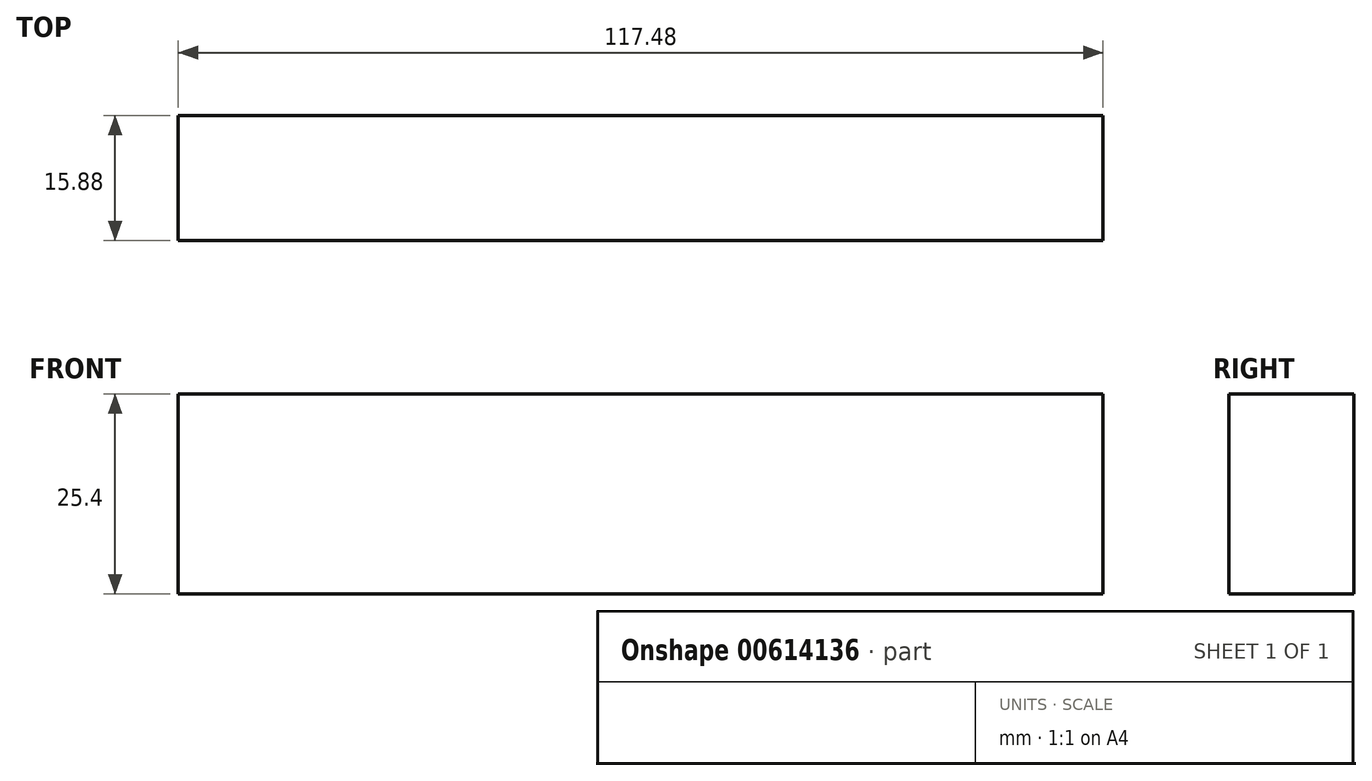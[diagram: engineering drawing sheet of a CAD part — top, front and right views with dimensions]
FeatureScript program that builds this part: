
annotation { "Feature Type Name" : "Feature", "Feature Type Description" : "" }
export const myFeature = defineFeature(function(context is Context, id is Id, definition is map)
    precondition{}
    {
        {
            var Q0;
            Q0=qCreatedBy(makeId("Top.planeOp"),FACE);
            var sketch = newSketch(context, id + "F0", { "sketchPlane" : qUnion([Q0])});
            skLineSegment(sketch, "E0.bottom", {"start": v(58.74, 7.94) * mm, "end": v(-58.74, 7.94) * mm});
            skLineSegment(sketch, "E0.top", {"start": v(58.74, -7.94) * mm, "end": v(-58.74, -7.94) * mm});
            skLineSegment(sketch, "E0.left", {"start": v(58.74, 7.94) * mm, "end": v(58.74, -7.94) * mm});
            skLineSegment(sketch, "E0.right", {"start": v(-58.74, 7.94) * mm, "end": v(-58.74, -7.94) * mm});
            skPoint(sketch, "E0.middle", {"position": v(0, 0) * mm});
            skSolve(sketch);
        }
        {
            var Q0;
            Q0=makeQuery(id+"F0.imprint","IMPRINT",FACE,{"disambiguationData":[TD([[makeQuery(id+"F0.imprint","IMPRINT",EDGE,{"derivedFrom":sQuery(id+"F0.wireOp",EDGE,"E0.bottom")}),1.0]])]});
            extrude(context, id + "F1", {"entities" : qUnion([Q0]), "depth" : 25.4 * mm, "offsetDistance" : 25.4 * mm});
        }
    });
